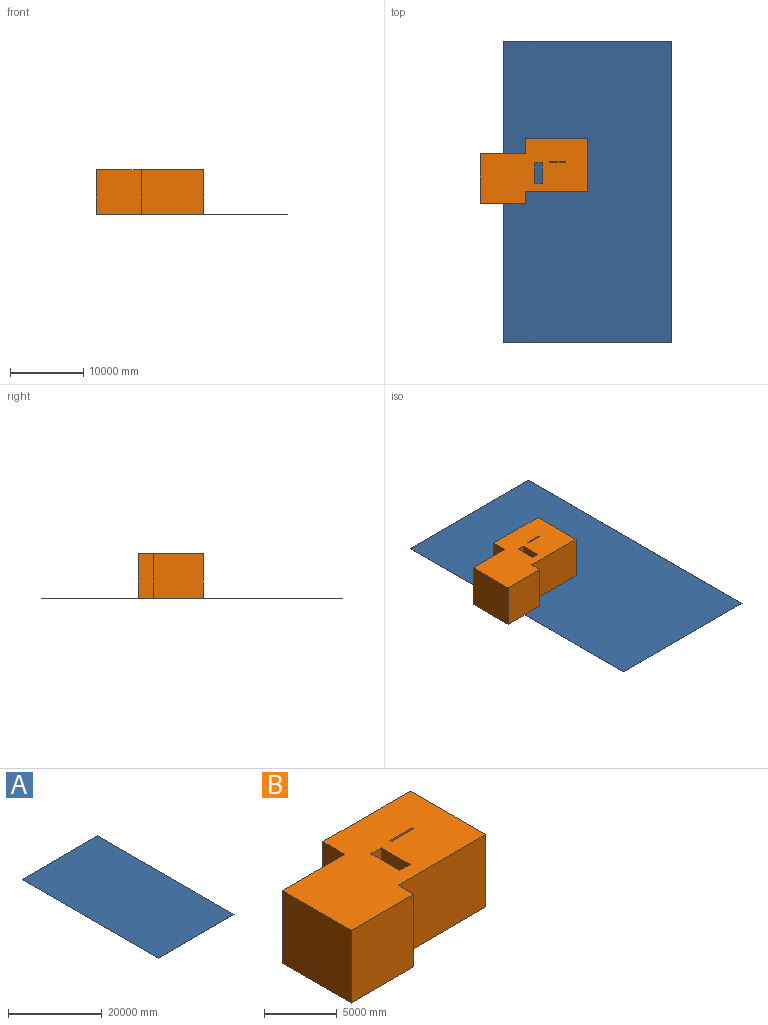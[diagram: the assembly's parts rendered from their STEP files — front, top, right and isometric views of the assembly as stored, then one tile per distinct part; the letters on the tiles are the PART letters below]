
ASSEMBLY  parts=2 mates=2
PART A: 6 faces, bbox 22860x41148x25 mm
  f0: plane 41148x25mm, normal (1,0,0), area 1028700mm2, adj f1,f3,f4,f5
  f1: plane 22860x25mm, normal (0,1,0), area 571500mm2, adj f0,f2,f4,f5
  f2: plane 41148x25mm, normal (-1,0,0), area 1028700mm2, adj f1,f3,f4,f5
  f3: plane 22860x25mm, normal (0,-1,0), area 571500mm2, adj f0,f2,f4,f5
  f4: plane 41148x22860mm, normal (0,0,1), area 940643280mm2, adj f0,f1,f2,f3
  f5: plane 41148x22860mm, normal (0,0,-1), area 940643280mm2, adj f0,f1,f2,f3
PART B: 18 faces, bbox 14630.4x8839.2x6096 mm
  f0: plane 6096x2807.03mm, normal (-1,0,0), area 17111673.3mm2, adj f1,f15,f16,f17
  f1: plane 6096x1003.3mm, normal (0,1,0), area 6116116.8mm2, adj f0,f2,f16,f17
  f2: plane 6096x2807.03mm, normal (1,0,0), area 17111673.3mm2, adj f1,f15,f16,f17
  f3: plane 6096x2159mm, normal (0,-1,0), area 13161264mm2, adj f4,f13,f16,f17
  f4: plane 6096x127mm, normal (-1,0,0), area 774192mm2, adj f3,f5,f16,f17
  f5: plane 6096x2159mm, normal (0,1,0), area 13161264mm2, adj f4,f13,f16,f17
  f6: plane 6096x6096mm, normal (0,-1,0), area 37161216mm2, adj f7,f14,f16,f17
  f7: plane 6096x1524mm, normal (1,0,0), area 9290304mm2, adj f6,f8,f16,f17
  f8: plane 8534.4x6096mm, normal (0,-1,0), area 52025702.4mm2, adj f7,f9,f16,f17
  f9: plane 7315.2x6096mm, normal (1,0,0), area 44593459.2mm2, adj f8,f10,f16,f17
  f10: plane 8534.4x6096mm, normal (0,1,0), area 52025702.4mm2, adj f9,f11,f16,f17
  f11: plane 6096x2133.6mm, normal (-1,0,0), area 13006425.6mm2, adj f10,f12,f16,f17
  f12: plane 6096x6096mm, normal (0,1,0), area 37161216mm2, adj f11,f14,f16,f17
  f13: plane 6096x127mm, normal (1,0,0), area 774192mm2, adj f3,f5,f16,f17
  f14: plane 6705.6x6096mm, normal (-1,0,0), area 40877337.6mm2, adj f6,f12,f16,f17
  f15: plane 6096x1003.3mm, normal (0,-1,0), area 6116116.8mm2, adj f0,f2,f16,f17
  f16: plane 14630.4x8839.2mm, normal (0,0,1), area 100217691.2mm2, adj f0,f1,f2,f3,f4,f5,f6,f7
  f17: plane 14630.4x8839.2mm, normal (0,0,-1), area 100217691.2mm2, adj f0,f1,f2,f3,f4,f5,f6,f7
PLACE A at identity fixed
PLACE B t=(-4267.2,3657.6,25)mm
MATE planar A.f4 <-> A.f4  axis (0,0,1) through (0,0,25)mm
MATE planar B.f17 <-> A.f4  axis (0,0,1) through (0,0,25)mm
